# Revit family: ALN445 Post Top Mount
name_source: partatom
category: Lighting Fixtures
revit_build: Autodesk Revit MEP 2012 (Build: 20110309_2315(x64)
units: mm (PartAtom-declared; Revit-internal decimal feet)

## types (13) — shared parameters
Apparent Load = 100 VA
Default Elevation = 48.000"
Description = The Towne Commons family of fixtures are available in a wide range of sizes and configurations
Lamp = ED-28 & ED-23 1/2
Light Bulb Material = Hubbell - Glass
Load Classification = Lighting
Manufacturer = Architectural Area Lighting
Manufacturer Fax = (626)-369-2695
Model = ALN445
Product Documentation Link = http://cdn.aal.net
Product Page URL = http://www.aal.net
URL = http://www.aal.net
Wattage Comments = 70-400W

## per-type parameters (varying)
| type | Finish |
| Antique Green | Hubbell-Aluminum-Antique Green |
| Arctic White | Hubbell-Aluminum-Artic White |
| Black | Hubbell-Aluminum-Black |
| Matte Black | Hubbell-Aluminum-Matte Black |
| Dark Green | Hubbell-Aluminum-Dark Green |
| Dark Bronze | Hubbell-Aluminum-Dark Bronze |
| Weathered Bronze | Hubbell-Aluminum-Weathered Bronze |
| Metalic Bronze | Hubbell-Aluminum-Metalic Bronze |
| Verde Blue | Hubbell-Aluminum-Verde Blue |
| Corten | Hubbell-Aluminum-Corten |
| Matte Aluminum | Hubbell-Aluminum-Matte |
| Medium Grey | Hubbell-Aluminum-Medium Grey |
| Light Grey | Hubbell-Aluminum-Light Grey |

## geometry (parser evidence)
native form markers: Blend x16, Sweep x5
no freeform markers — native parametric forms only
